# Revit family: 64442210
name_source: partatom
category: Plumbing Fixtures
revit_build: Autodesk Revit 2016 (Build: 20150220_1215(x64)
units: mm (PartAtom-declared; Revit-internal decimal feet)

## family parameters
Always vertical = Yes
Cut with Voids When Loaded = No
OmniClass Number = 23.45.55.00
OmniClass Title = Sanitary Faucets, Wastes
Part Type = Normal
Room Calculation Point = No
Round Connector Dimension = Use Diameter
Shared = No
Work Plane-Based = No

## types (1)
- 64442210 Washbasin faucet, 6 V
    2D/3D/BIM Files URL = http://static.hansa.com
    Advanced Features = Without draw-rod opening
    Approval ACS = 15 ACC LY 337
    AssetType = Fixed
    BIMObjectName = 64442210
    Battery = Lithium 2CR5 6 V
    BodyMaterial = Brass
    Brand = Hansa
    Catalog Drawing URL = http://static.hansa.com
    Category = Bathroom, public & semi-public
    Class = Battery-operated, touchless
    CloseOffRating = 0
    Color = Chrome
    Connection Size = G3/8
    ConvergoRefNr = 0087-1809-0153-FI
    Customs Code = 84818011
    DN Size = DN15
    Dimension Drawing URL = http://static.hansa.com
    DurationUnit = Year
    EAN Number = 4015474273344
    EMC Directive = 2004/108/EY
    ETA-Danmark = VA 1.42/19925
    Electronic Parts = Solenoid valve, infrared sensor
    Extensions = No pop-up waste included
    FDV Document URL = http://www.hansa.com
    FaucetMainMaterial = Brass
    Features = Battery-operated, touchless
    Finish = Polished
    Flow Drawing URL = http://static.hansa.com
    Flow Rate At 300kPa = 0.1 L/s
    FlowCoefficient = 0
    Group = Washbasin faucets
    Health Sales Arguments = Touch-free operation. Maximum comfort, maximum hygiene.
    IfcExportAs = IfcValveType
    IfcExportType = FAUCET
    InletConnectionSize = 16 mm  [stored 0.0524934 ft]
    Installation Type = Deck mounted
    Installation and Maintenance = http://static.hansa.com
    Intelligent After Flow Period = 2 s ± 1 s
    Lever Handle = Temperature control handle
    ManufacterURL = http://www.hansa.com
    Manufacturer = Hansa
    ManufacturerName = Hansa
    Market = AUT;BEL;CZE;DEU;ESP;FRA;INT;ITA;NLD;SVK
    Material = Brass
    Max Flow Period = 120.0 s
    Max. Hot Water Supply = 70 °C
    Mechanical Parts = Litter filter(s)
    Model = 64442210 Washbasin faucet, 6 V
    ModelReference = 64442210
    Mounting Holes = 1 mounting hole
    NBSDescription = Water supply fittings for wash basins and troughs
    NBSReference = 45-35-70/371
    Name = 64442210 Washbasin faucet, 6 V
    Name_en = 64442210 Washbasin faucet, 6 V
    Noise Class = I (ISO 3822)
    NominalDepth = 212 mm
    NominalHeight = 293 mm
    NominalWidth = 72 mm
    Operating Voltage = 6 V
    Package Weight = 2.26 kg
    Package external Dimensions = 695 x 320 x 85
    Pipes = Flexible inlet pipe(s)
    Pressure Loss With Flow 01ls = 200000.0 Pa
    Product Code = 64442210
    Product Datasheet = http://www.hansa.com
    Product Family = HANSAELECTRA
    Product Image URL = http://static.hansa.com
    Product URL = http://static.hansa.com
    Projection = 170 mm  [stored 0.557743 ft]
    Protection Class = IP 55
    Recognition Range = optimally preset
    Revision = 2
    STF Certificate = STF VTT-RTH-00031-11
    Shape = Sculptured
    Size = 75x215x295 mm
    Spare Parts = http://static.hansa.com
    Spout Type = Fixed spout
    Temperature = Temperature fixable, temperature regulator
    URL ACS = http://static.hansa.com
    URL ETA-Danmark = http://static.hansa.com
    URL STF = http://static.hansa.com
    Uniclass2 = Pr_40_30_96_07
    Uniclass2015Description = Bath manual water supply sets
    Uniclass2015Reference = Pr_40_20_87_07
    Usage Group = Offices, personnel sanitary facilities;Pharmacies, Opticians, Dentists;Health centers & Child welfare clinics;Households
    Version = 2
    VersionDate = 01/01/2019
    WarrantyDescription = http://warranty.hansa.com
    WarrantyDurationUnit = Year
    WorkingPressure = 100 - 1000 kPa

note: [stored X ft] marks values corroborated as IEEE doubles in the binary element streams (Revit-internal decimal feet)

## geometry (parser evidence)
native form markers: Sweep x6
no freeform markers — native parametric forms only
